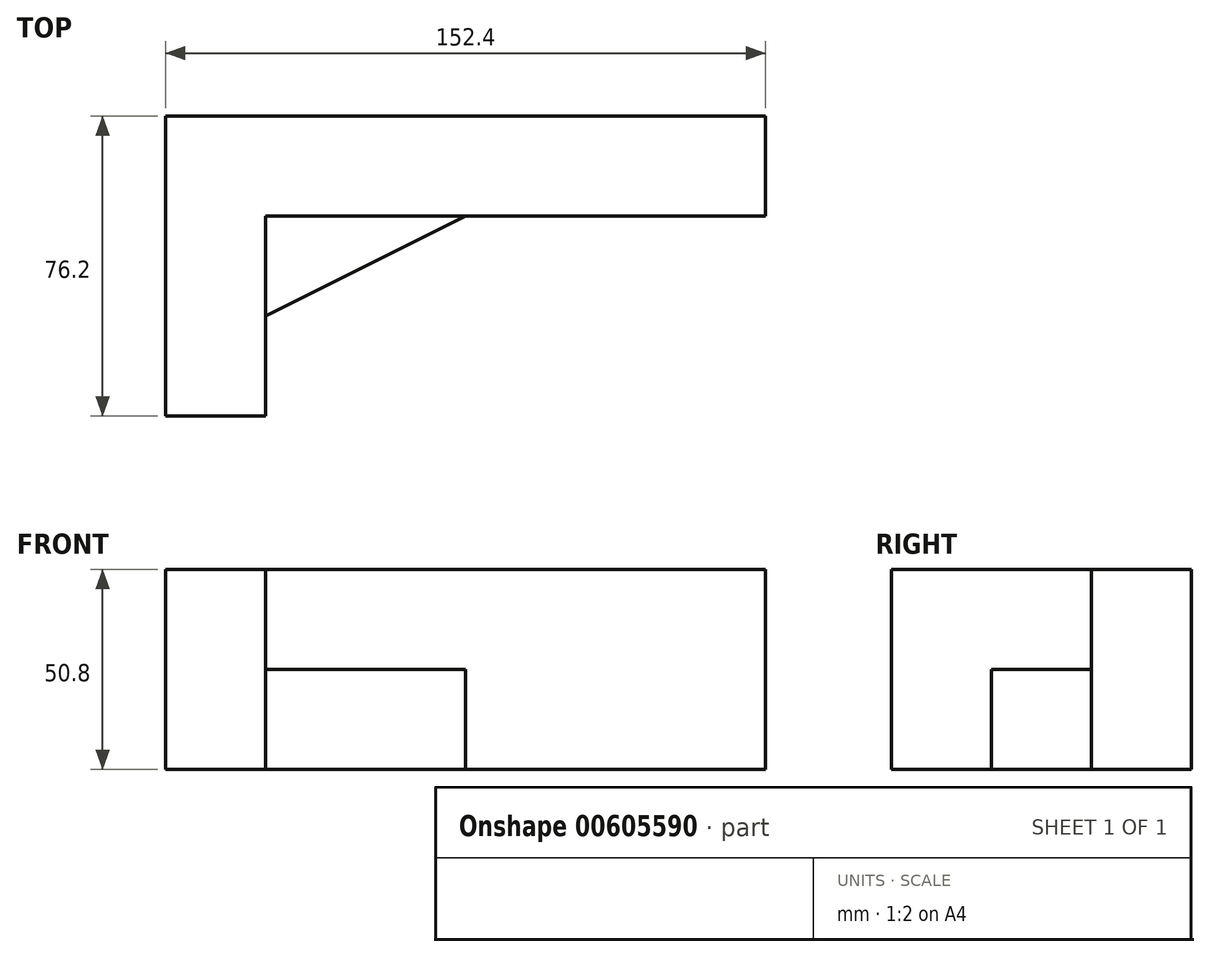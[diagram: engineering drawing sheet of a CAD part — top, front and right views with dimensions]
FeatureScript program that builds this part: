
annotation { "Feature Type Name" : "Feature", "Feature Type Description" : "" }
export const myFeature = defineFeature(function(context is Context, id is Id, definition is map)
    precondition{}
    {
        {
            var Q0;
            Q0=qCreatedBy(makeId("Front.planeOp"),FACE);
            var sketch = newSketch(context, id + "F0", { "sketchPlane" : qUnion([Q0])});
            skLineSegment(sketch, "E0", {"start": v(0, 0) * mm, "end": v(152.4, 0) * mm});
            skLineSegment(sketch, "E1", {"start": v(152.4, 0) * mm, "end": v(152.4, 50.8) * mm});
            skLineSegment(sketch, "E2", {"start": v(152.4, 50.8) * mm, "end": v(0, 50.8) * mm});
            skLineSegment(sketch, "E3", {"start": v(0, 50.8) * mm, "end": v(0, 0) * mm});
            skSolve(sketch);
        }
        {
            var Q0;
            Q0=makeQuery(id+"F0.imprint","IMPRINT",FACE,{"disambiguationData":[TD([[makeQuery(id+"F0.imprint","IMPRINT",EDGE,{"derivedFrom":sQuery(id+"F0.wireOp",EDGE,"E0")}),1.0]])]});
            extrude(context, id + "F1", {"entities" : qUnion([Q0]), "depth" : 76.2 * mm, "offsetDistance" : 25.4 * mm});
        }
        {
            var Q0;
            Q0=makeQuery(id+"F1.opExtrude","CAP_FACE",FACE,{"disambiguationData":[OSD([sQuery(id+"F0.wireOp",EDGE,"E0"),sQuery(id+"F0.wireOp",EDGE,"E1"),sQuery(id+"F0.wireOp",EDGE,"E2"),sQuery(id+"F0.wireOp",EDGE,"E3")])],"isStart":false});
            var sketch = newSketch(context, id + "F2", { "sketchPlane" : qUnion([Q0])});
            skLineSegment(sketch, "E4", {"start": v(152.4, 50.8) * mm, "end": v(25.4, 50.8) * mm});
            skLineSegment(sketch, "E5", {"start": v(25.4, 50.8) * mm, "end": v(25.4, 0) * mm});
            skLineSegment(sketch, "E6", {"start": v(25.4, 0) * mm, "end": v(152.4, 0) * mm});
            skLineSegment(sketch, "E7", {"start": v(152.4, 0) * mm, "end": v(152.4, 50.8) * mm});
            skSolve(sketch);
        }
        {
            var Q0;
            Q0=makeQuery(id+"F2.imprint","IMPRINT",FACE,{"disambiguationData":[TD([[makeQuery(id+"F2.imprint","IMPRINT",EDGE,{"derivedFrom":sQuery(id+"F2.wireOp",EDGE,"E4")}),1.0]])]});
            extrude(context, id + "F3", {"entities" : qUnion([Q0]), "operationType" : NewBodyOperationType.REMOVE, "oppositeDirection" : true, "depth" : 50.8 * mm, "offsetDistance" : 25.4 * mm});
        }
        {
            var Q0;
            Q0=makeQuery(id+"F3.boolean.opBoolean","COPY",FACE,{"derivedFrom":makeQuery(id+"F3.opExtrude","CAP_FACE",FACE,{"disambiguationData":[OSD([sQuery(id+"F2.wireOp",EDGE,"E4"),sQuery(id+"F2.wireOp",EDGE,"E5"),sQuery(id+"F2.wireOp",EDGE,"E6"),sQuery(id+"F2.wireOp",EDGE,"E7")])],"isStart":false})});
            var sketch = newSketch(context, id + "F4", { "sketchPlane" : qUnion([Q0])});
            skLineSegment(sketch, "E8", {"start": v(25.4, 0) * mm, "end": v(25.4, 25.4) * mm});
            skLineSegment(sketch, "E9", {"start": v(25.4, 25.4) * mm, "end": v(76.2, 25.4) * mm});
            skLineSegment(sketch, "E10", {"start": v(76.2, 25.4) * mm, "end": v(76.2, 0) * mm});
            skLineSegment(sketch, "E11", {"start": v(76.2, 0) * mm, "end": v(25.4, 0) * mm});
            skSolve(sketch);
        }
        {
            var Q0;
            Q0=makeQuery(id+"F4.imprint","IMPRINT",FACE,{"disambiguationData":[TD([[makeQuery(id+"F4.imprint","IMPRINT",EDGE,{"derivedFrom":sQuery(id+"F4.wireOp",EDGE,"E8")}),1.0]])]});
            extrude(context, id + "F5", {"entities" : qUnion([Q0]), "operationType" : NewBodyOperationType.ADD, "depth" : 25.4 * mm, "offsetDistance" : 25.4 * mm});
        }
        {
            var Q0;
            Q0=makeQuery(id+"F5.opExtrude","SWEPT_FACE",FACE,{"disambiguationData":[OSD([sQuery(id+"F4.wireOp",EDGE,"E9")])]});
            var sketch = newSketch(context, id + "F6", { "sketchPlane" : qUnion([Q0])});
            skLineSegment(sketch, "E12", {"start": v(76.2, -25.4) * mm, "end": v(25.4, -50.8) * mm});
            skLineSegment(sketch, "E13", {"start": v(25.4, -50.8) * mm, "end": v(76.2, -50.8) * mm});
            skLineSegment(sketch, "E14", {"start": v(76.2, -50.8) * mm, "end": v(76.2, -25.4) * mm});
            skSolve(sketch);
        }
        {
            var Q0;
            Q0=makeQuery(id+"F6.imprint","IMPRINT",FACE,{"disambiguationData":[TD([[makeQuery(id+"F6.imprint","IMPRINT",EDGE,{"derivedFrom":sQuery(id+"F6.wireOp",EDGE,"E12")}),1.0]])]});
            extrude(context, id + "F7", {"entities" : qUnion([Q0]), "operationType" : NewBodyOperationType.REMOVE, "oppositeDirection" : true, "depth" : 25.4 * mm, "offsetDistance" : 25.4 * mm});
        }
    });
